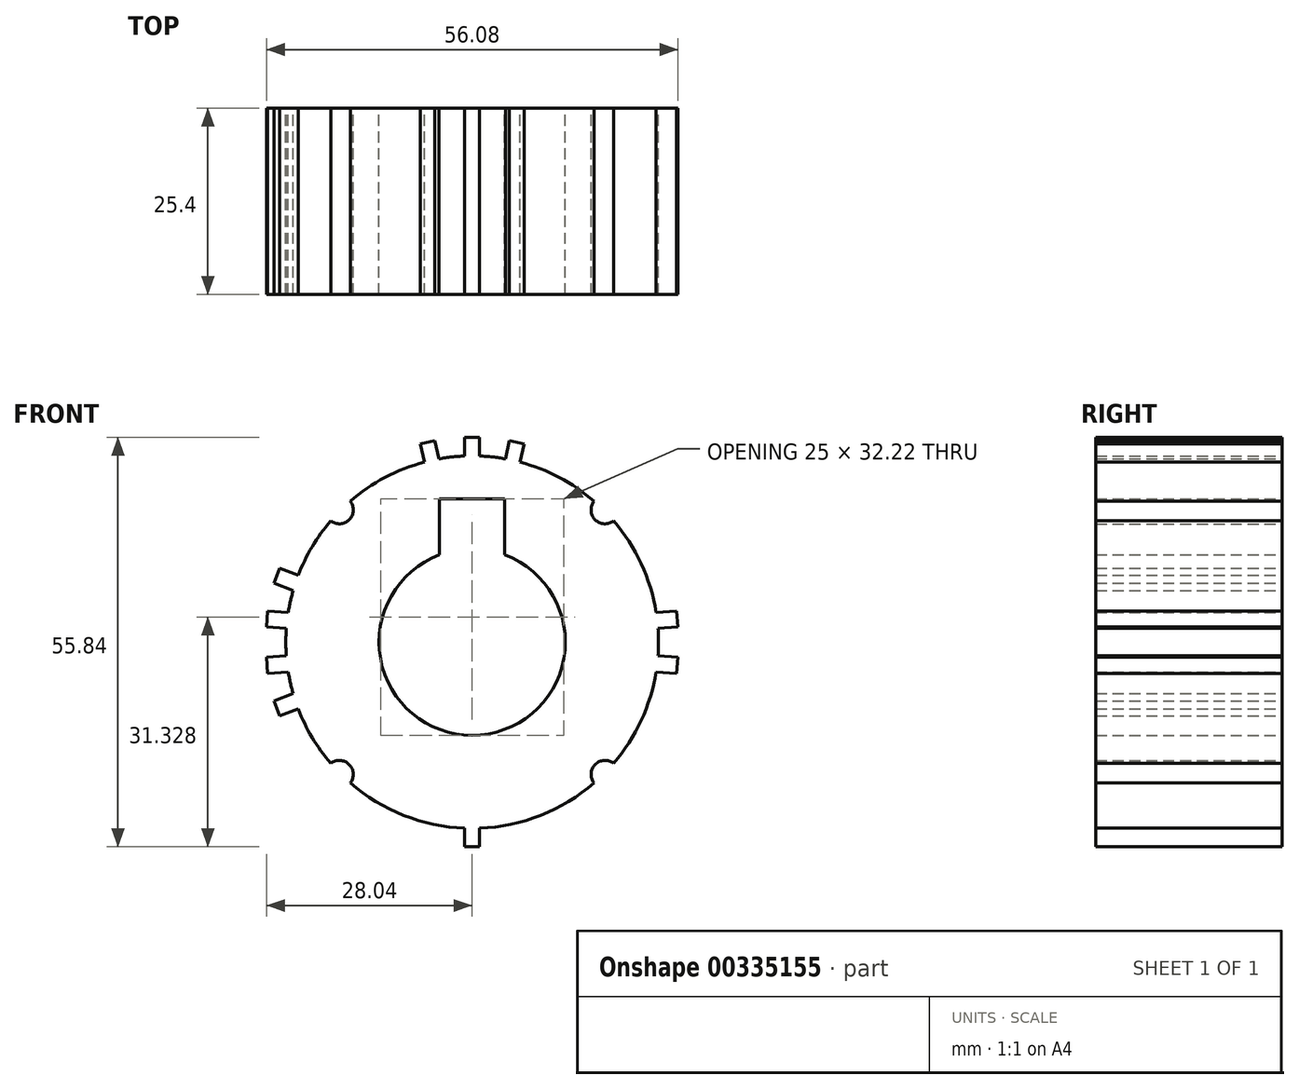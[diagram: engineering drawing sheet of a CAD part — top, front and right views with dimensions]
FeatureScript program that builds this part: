
annotation { "Feature Type Name" : "Feature", "Feature Type Description" : "" }
export const myFeature = defineFeature(function(context is Context, id is Id, definition is map)
    precondition{}
    {
        {
            var Q0;
            Q0=qCreatedBy(makeId("Front.planeOp"),FACE);
            var sketch = newSketch(context, id + "F0", { "sketchPlane" : qUnion([Q0])});
            skArc(sketch, "E0", {"start": v(16.62, 19.21) * mm, "mid": v(11.87, 22.46) * mm, "end": v(6.52, 24.55) * mm});
            skArc(sketch, "E1", {"start": v(-4.44, 11.9) * mm, "mid": v(0, -12.7) * mm, "end": v(4.44, 11.9) * mm});
            skLineSegment(sketch, "E2", {"start": v(-4.44, 11.9) * mm, "end": v(-4.44, 19.52) * mm});
            skLineSegment(sketch, "E3.MirrorCS", {"start": v(4.45, 11.9) * mm, "end": v(4.45, 19.52) * mm});
            skLineSegment(sketch, "E4", {"start": v(-4.44, 19.52) * mm, "end": v(4.44, 19.52) * mm});
            skArc(sketch, "E5", {"start": v(16.62, 19.21) * mm, "mid": v(16.76, 16.69) * mm, "end": v(19.28, 16.53) * mm});
            skPoint(sketch, "E6.end.orphan", {"position": v(0, 38.1) * mm});
            skPoint(sketch, "E7.end.orphan", {"position": v(38.1, 0) * mm});
            skArc(sketch, "E8.MirrorCS", {"start": v(-16.62, 19.21) * mm, "mid": v(-16.76, 16.69) * mm, "end": v(-19.28, 16.53) * mm});
            skArc(sketch, "E9.MirrorCS", {"start": v(16.62, -19.21) * mm, "mid": v(16.76, -16.69) * mm, "end": v(19.28, -16.53) * mm});
            skArc(sketch, "E10.MirrorCS", {"start": v(-16.62, -19.21) * mm, "mid": v(-16.76, -16.69) * mm, "end": v(-19.28, -16.53) * mm});
            skArc(sketch, "E11.trimOffspring", {"start": v(19.28, -16.53) * mm, "mid": v(23.04, -10.7) * mm, "end": v(25.07, -4.06) * mm});
            skArc(sketch, "E12.trimOffspring", {"start": v(-19.28, 16.53) * mm, "mid": v(-21.82, 13) * mm, "end": v(-23.71, 9.1) * mm});
            skArc(sketch, "E13.trimOffspring", {"start": v(-16.62, -19.21) * mm, "mid": v(-9.34, -23.62) * mm, "end": v(-1.02, -25.38) * mm});
            skLineSegment(sketch, "E14", {"start": v(1.02, 25.38) * mm, "end": v(1.02, 27.92) * mm});
            skLineSegment(sketch, "E15.MirrorCS", {"start": v(-1.02, 25.38) * mm, "end": v(-1.02, 27.92) * mm});
            skLineSegment(sketch, "E16", {"start": v(1.02, 27.92) * mm, "end": v(-1.02, 27.92) * mm});
            skArc(sketch, "E17.trimOffspring", {"start": v(-1.02, 25.38) * mm, "mid": v(-2.78, 25.25) * mm, "end": v(-4.53, 25) * mm});
            skLineSegment(sketch, "E18.MirrorCS", {"start": v(4.53, 25) * mm, "end": v(5.09, 27.47) * mm});
            skLineSegment(sketch, "E19.MirrorCS", {"start": v(5.09, 27.47) * mm, "end": v(7.07, 27.03) * mm});
            skLineSegment(sketch, "E20.MirrorCS", {"start": v(6.52, 24.55) * mm, "end": v(7.07, 27.03) * mm});
            skLineSegment(sketch, "E21.MirrorCS", {"start": v(-4.53, 25) * mm, "end": v(-5.09, 27.47) * mm});
            skLineSegment(sketch, "E22.MirrorCS", {"start": v(-6.52, 24.55) * mm, "end": v(-7.07, 27.03) * mm});
            skLineSegment(sketch, "E23.MirrorCS", {"start": v(-5.09, 27.47) * mm, "end": v(-7.07, 27.03) * mm});
            skArc(sketch, "E24.trimOffspring", {"start": v(4.53, 25) * mm, "mid": v(2.78, 25.25) * mm, "end": v(1.02, 25.38) * mm});
            skArc(sketch, "E25.trimOffspring", {"start": v(-6.52, 24.55) * mm, "mid": v(-11.87, 22.46) * mm, "end": v(-16.62, 19.21) * mm});
            skLineSegment(sketch, "E26.MirrorCS", {"start": v(1.02, -25.38) * mm, "end": v(1.02, -27.92) * mm});
            skLineSegment(sketch, "E27.MirrorCS", {"start": v(1.02, -27.92) * mm, "end": v(-1.02, -27.92) * mm});
            skLineSegment(sketch, "E28.MirrorCS", {"start": v(-1.02, -25.38) * mm, "end": v(-1.02, -27.92) * mm});
            skArc(sketch, "E29.trimOffspring", {"start": v(1.02, -25.38) * mm, "mid": v(9.34, -23.62) * mm, "end": v(16.62, -19.21) * mm});
            skLineSegment(sketch, "E30", {"start": v(28.04, -2.06) * mm, "end": v(27.88, -4.26) * mm});
            skLineSegment(sketch, "E31", {"start": v(27.88, -4.26) * mm, "end": v(25.07, -4.06) * mm});
            skLineSegment(sketch, "E32.trimOffspring", {"start": v(25.33, -1.86) * mm, "end": v(28.04, -2.06) * mm});
            skArc(sketch, "E33.trimOffspring", {"start": v(25.33, -1.86) * mm, "mid": v(25.4, 0) * mm, "end": v(25.33, 1.86) * mm});
            skLineSegment(sketch, "E34.MirrorCS", {"start": v(25.33, 1.86) * mm, "end": v(28.04, 2.06) * mm});
            skLineSegment(sketch, "E35.MirrorCS", {"start": v(28.04, 2.06) * mm, "end": v(27.88, 4.26) * mm});
            skLineSegment(sketch, "E36.MirrorCS", {"start": v(27.88, 4.26) * mm, "end": v(25.07, 4.06) * mm});
            skArc(sketch, "E37.trimOffspring", {"start": v(25.07, 4.06) * mm, "mid": v(23.04, 10.7) * mm, "end": v(19.28, 16.53) * mm});
            skLineSegment(sketch, "E38.MirrorCS", {"start": v(-27.88, -4.26) * mm, "end": v(-25.07, -4.06) * mm});
            skLineSegment(sketch, "E39.MirrorCS", {"start": v(-28.04, -2.06) * mm, "end": v(-27.88, -4.26) * mm});
            skLineSegment(sketch, "E40.MirrorCS", {"start": v(-25.33, -1.86) * mm, "end": v(-28.04, -2.06) * mm});
            skLineSegment(sketch, "E41.MirrorCS", {"start": v(-25.33, 1.86) * mm, "end": v(-28.04, 2.06) * mm});
            skLineSegment(sketch, "E42.MirrorCS", {"start": v(-28.04, 2.06) * mm, "end": v(-27.88, 4.26) * mm});
            skLineSegment(sketch, "E43.MirrorCS", {"start": v(-27.88, 4.26) * mm, "end": v(-25.07, 4.06) * mm});
            skLineSegment(sketch, "E44.MirrorCS", {"start": v(-27.04, -8.02) * mm, "end": v(-24.41, -7.01) * mm});
            skLineSegment(sketch, "E45.MirrorCS", {"start": v(-26.25, -10.08) * mm, "end": v(-27.04, -8.02) * mm});
            skLineSegment(sketch, "E46.MirrorCS", {"start": v(-23.71, -9.1) * mm, "end": v(-26.25, -10.08) * mm});
            skArc(sketch, "E47.trimOffspring", {"start": v(-23.71, -9.1) * mm, "mid": v(-21.82, -13) * mm, "end": v(-19.28, -16.53) * mm});
            skArc(sketch, "E48.trimOffspring", {"start": v(-25.07, -4.06) * mm, "mid": v(-24.79, -5.54) * mm, "end": v(-24.41, -7.01) * mm});
            skArc(sketch, "E49.trimOffspring", {"start": v(-25.33, 1.86) * mm, "mid": v(-25.4, 0) * mm, "end": v(-25.33, -1.86) * mm});
            skLineSegment(sketch, "E50.MirrorCS", {"start": v(-27.04, 8.02) * mm, "end": v(-24.41, 7.01) * mm});
            skLineSegment(sketch, "E51.MirrorCS", {"start": v(-26.25, 10.08) * mm, "end": v(-27.04, 8.02) * mm});
            skLineSegment(sketch, "E52.MirrorCS", {"start": v(-23.71, 9.1) * mm, "end": v(-26.25, 10.08) * mm});
            skArc(sketch, "E53.trimOffspring", {"start": v(-24.41, 7.01) * mm, "mid": v(-24.79, 5.54) * mm, "end": v(-25.07, 4.06) * mm});
            skSolve(sketch);
        }
        {
            var Q0;
            Q0 = qSketchRegion(id + "F0", true);
            extrude(context, id + "F1", {"entities" : qUnion([Q0]), "depth" : 25.4 * mm, "offsetDistance" : 25.4 * mm});
        }
    });
